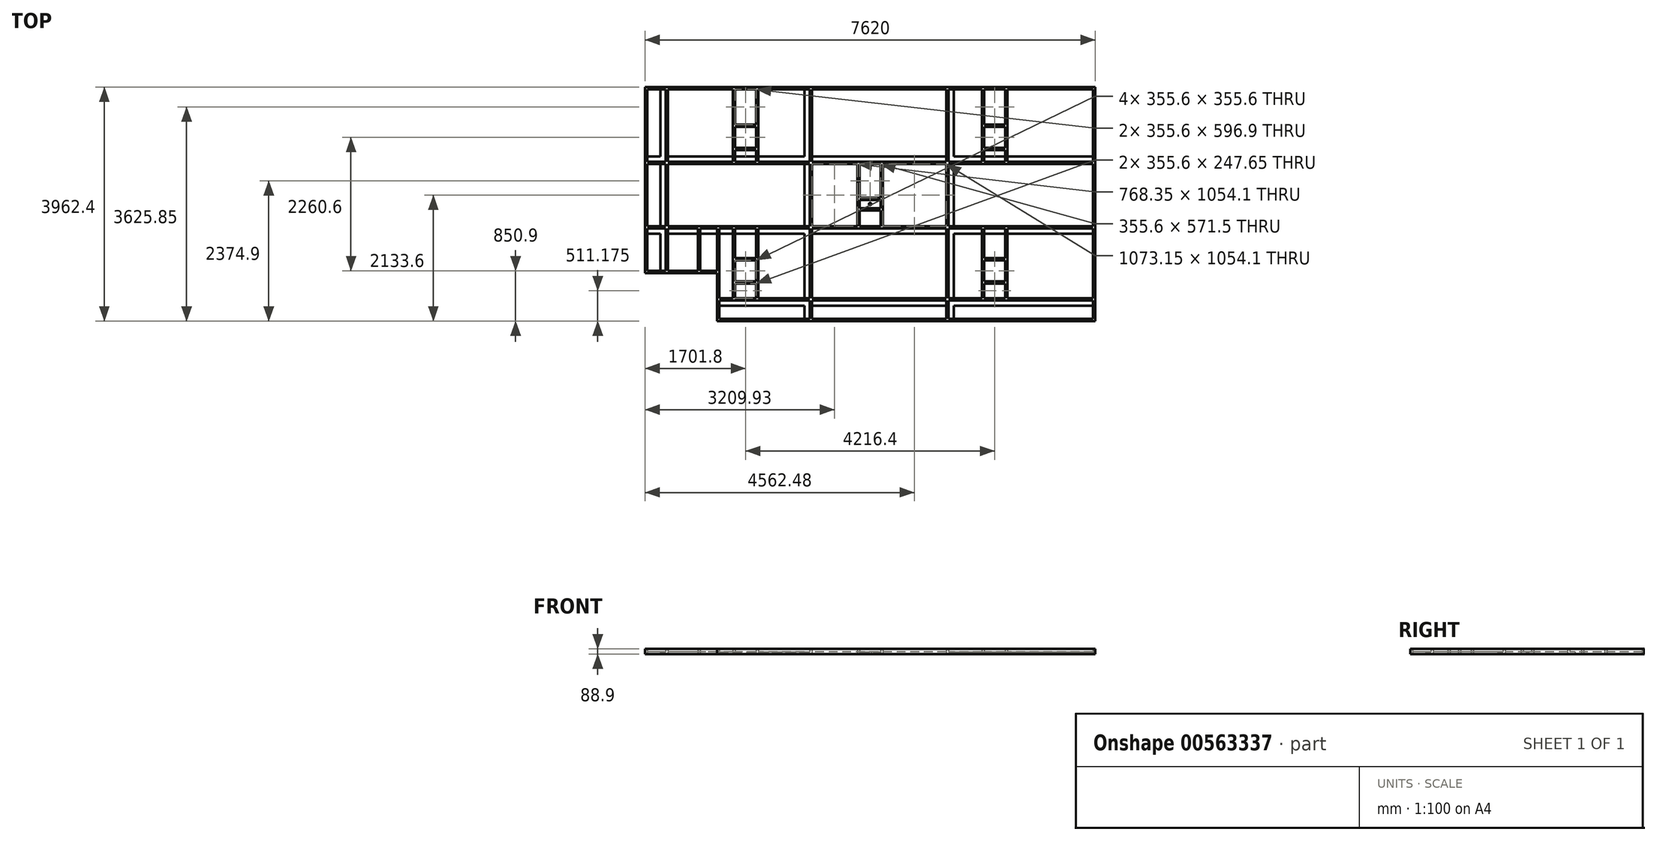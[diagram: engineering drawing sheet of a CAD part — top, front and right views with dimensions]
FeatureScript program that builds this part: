
annotation { "Feature Type Name" : "Feature", "Feature Type Description" : "" }
export const myFeature = defineFeature(function(context is Context, id is Id, definition is map)
    precondition{}
    {
        {
            var Q0;
            Q0=qCreatedBy(makeId("Top.planeOp"),FACE);
            var sketch = newSketch(context, id + "F0", { "sketchPlane" : qUnion([Q0])});
            skLineSegment(sketch, "E0", {"start": v(-2590.8, -1168.4) * mm, "end": v(-3810, -1168.4) * mm});
            skLineSegment(sketch, "E1", {"start": v(-3810, -1168.4) * mm, "end": v(-3810, 1981.2) * mm});
            skLineSegment(sketch, "E2", {"start": v(-3810, 1981.2) * mm, "end": v(3810, 1981.2) * mm});
            skLineSegment(sketch, "E3", {"start": v(3810, 1981.2) * mm, "end": v(3810, -1981.2) * mm});
            skLineSegment(sketch, "E4", {"start": v(3810, -1981.2) * mm, "end": v(-2590.8, -1981.2) * mm});
            skLineSegment(sketch, "E5", {"start": v(-2590.8, -1981.2) * mm, "end": v(-2590.8, -1168.4) * mm});
            skLineSegment(sketch, "E6", {"start": v(0, 0) * mm, "end": v(0, 3581.3) * mm, "construction": true});
            skLineSegment(sketch, "E7", {"start": v(0, 0) * mm, "end": v(6897.1, 0) * mm, "construction": true});
            skLineSegment(sketch, "E8", {"start": v(3810, 762) * mm, "end": v(-3810, 762) * mm, "construction": true});
            skLineSegment(sketch, "E9", {"start": v(3810, -457.2) * mm, "end": v(-3810, -457.2) * mm, "construction": true});
            skLineSegment(sketch, "E10", {"start": v(-2590.8, -1676.4) * mm, "end": v(3810, -1676.4) * mm, "construction": true});
            skLineSegment(sketch, "E11.0", {"start": v(3771.9, 806.45) * mm, "end": v(1416.05, 806.45) * mm});
            skLineSegment(sketch, "E12.0", {"start": v(3771.9, 717.55) * mm, "end": v(1416.05, 717.55) * mm});
            skLineSegment(sketch, "E13.0", {"start": v(3771.9, -501.65) * mm, "end": v(1416.05, -501.65) * mm});
            skLineSegment(sketch, "E14.0", {"start": v(3771.9, -412.75) * mm, "end": v(1416.05, -412.75) * mm});
            skLineSegment(sketch, "E15.0", {"start": v(-2590.8, -1720.85) * mm, "end": v(-1111.25, -1720.85) * mm});
            skLineSegment(sketch, "E16.0", {"start": v(-2590.8, -1631.95) * mm, "end": v(-1111.25, -1631.95) * mm});
            skLineSegment(sketch, "E17.0", {"start": v(-3810, 1943.1) * mm, "end": v(3771.9, 1943.1) * mm});
            skLineSegment(sketch, "E18.0", {"start": v(3771.9, 1943.1) * mm, "end": v(3771.9, -1943.1) * mm});
            skLineSegment(sketch, "E19.0", {"start": v(3771.9, -1943.1) * mm, "end": v(-2590.8, -1943.1) * mm});
            skLineSegment(sketch, "E20", {"start": v(1371.6, 1943.1) * mm, "end": v(1371.6, -1943.1) * mm, "construction": true});
            skLineSegment(sketch, "E21", {"start": v(3771.9, -1943.1) * mm, "end": v(3810, -1943.1) * mm});
            skLineSegment(sketch, "E22", {"start": v(3771.9, 1943.1) * mm, "end": v(3810, 1943.1) * mm});
            skLineSegment(sketch, "E23.0", {"start": v(-1066.8, 1943.1) * mm, "end": v(-1066.8, -1943.1) * mm, "construction": true});
            skLineSegment(sketch, "E24.0", {"start": v(-3505.2, 1943.1) * mm, "end": v(-3505.2, -1168.4) * mm, "construction": true});
            skLineSegment(sketch, "E25.0", {"start": v(-1111.25, 1943.1) * mm, "end": v(-1111.25, -1943.1) * mm});
            skLineSegment(sketch, "E26.0", {"start": v(-1022.35, 1943.1) * mm, "end": v(-1022.35, -1943.1) * mm});
            skLineSegment(sketch, "E27.0", {"start": v(1327.15, 1943.1) * mm, "end": v(1327.15, -1943.1) * mm});
            skLineSegment(sketch, "E28.0", {"start": v(1416.05, 1943.1) * mm, "end": v(1416.05, -1943.1) * mm});
            skLineSegment(sketch, "E29.0", {"start": v(-3549.65, 1943.1) * mm, "end": v(-3549.65, -1168.4) * mm});
            skLineSegment(sketch, "E30.0", {"start": v(-3460.75, 1943.1) * mm, "end": v(-3460.75, -1168.4) * mm});
            skLineSegment(sketch, "E31.trimOffspring", {"start": v(-1111.25, 806.45) * mm, "end": v(-3460.75, 806.45) * mm});
            skLineSegment(sketch, "E32.trimOffspring", {"start": v(-1111.25, 717.55) * mm, "end": v(-3460.75, 717.55) * mm});
            skLineSegment(sketch, "E33.trimOffspring", {"start": v(-1111.25, -412.75) * mm, "end": v(-3460.75, -412.75) * mm});
            skLineSegment(sketch, "E34.trimOffspring", {"start": v(-1111.25, -501.65) * mm, "end": v(-3460.75, -501.65) * mm});
            skLineSegment(sketch, "E35.trimOffspring", {"start": v(-1022.35, -1631.95) * mm, "end": v(1327.15, -1631.95) * mm});
            skLineSegment(sketch, "E36.trimOffspring", {"start": v(-1022.35, -1720.85) * mm, "end": v(1327.15, -1720.85) * mm});
            skLineSegment(sketch, "E37.trimOffspring", {"start": v(1289.05, 806.45) * mm, "end": v(-984.25, 806.45) * mm});
            skLineSegment(sketch, "E38.trimOffspring", {"start": v(1289.05, 717.55) * mm, "end": v(-984.25, 717.55) * mm});
            skLineSegment(sketch, "E39.trimOffspring", {"start": v(1327.15, -412.75) * mm, "end": v(-984.25, -412.75) * mm});
            skLineSegment(sketch, "E40.trimOffspring", {"start": v(1327.15, -501.65) * mm, "end": v(-984.25, -501.65) * mm});
            skLineSegment(sketch, "E41.trimOffspring", {"start": v(1416.05, -1631.95) * mm, "end": v(3771.9, -1631.95) * mm});
            skLineSegment(sketch, "E42.trimOffspring", {"start": v(1416.05, -1720.85) * mm, "end": v(3771.9, -1720.85) * mm});
            skLineSegment(sketch, "E43.trimOffspring", {"start": v(-3549.65, -412.75) * mm, "end": v(-3810, -412.75) * mm});
            skLineSegment(sketch, "E44.trimOffspring", {"start": v(-3549.65, -501.65) * mm, "end": v(-3810, -501.65) * mm});
            skLineSegment(sketch, "E45.trimOffspring", {"start": v(-3549.65, 806.45) * mm, "end": v(-3810, 806.45) * mm});
            skLineSegment(sketch, "E46.trimOffspring", {"start": v(-3549.65, 717.55) * mm, "end": v(-3810, 717.55) * mm});
            skLineSegment(sketch, "E47.0", {"start": v(-3771.9, -1130.3) * mm, "end": v(-3771.9, 1981.2) * mm});
            skLineSegment(sketch, "E47.1", {"start": v(-2552.7, -1130.3) * mm, "end": v(-3771.9, -1130.3) * mm});
            skLineSegment(sketch, "E47.2", {"start": v(-2552.7, -1981.2) * mm, "end": v(-2552.7, -1130.3) * mm});
            skLineSegment(sketch, "E48.0", {"start": v(-984.25, 1943.1) * mm, "end": v(-984.25, -1943.1) * mm});
            skLineSegment(sketch, "E49.0", {"start": v(3771.9, 679.45) * mm, "end": v(1416.05, 679.45) * mm});
            skLineSegment(sketch, "E50.0", {"start": v(1289.05, 679.45) * mm, "end": v(-984.25, 679.45) * mm});
            skLineSegment(sketch, "E51.0", {"start": v(1289.05, 1943.1) * mm, "end": v(1289.05, -1943.1) * mm});
            skLineSegment(sketch, "E52.0", {"start": v(-1111.25, 679.45) * mm, "end": v(-3397.25, 679.45) * mm});
            skLineSegment(sketch, "E53.0", {"start": v(-3549.65, 679.45) * mm, "end": v(-3810, 679.45) * mm});
            skLineSegment(sketch, "E54.0", {"start": v(1327.15, -374.65) * mm, "end": v(-984.25, -374.65) * mm});
            skLineSegment(sketch, "E55.0", {"start": v(3771.9, -374.65) * mm, "end": v(1416.05, -374.65) * mm});
            skLineSegment(sketch, "E56.0", {"start": v(-1111.25, -374.65) * mm, "end": v(-3397.25, -374.65) * mm});
            skLineSegment(sketch, "E57", {"start": v(-3549.65, 717.55) * mm, "end": v(-3460.75, 717.55) * mm});
            skLineSegment(sketch, "E58", {"start": v(-3549.65, 679.45) * mm, "end": v(-3397.25, 679.45) * mm});
            skLineSegment(sketch, "E59", {"start": v(-3549.65, -374.65) * mm, "end": v(-3810, -374.65) * mm});
            skLineSegment(sketch, "E60.0", {"start": v(-2590.8, -1593.85) * mm, "end": v(-1111.25, -1593.85) * mm});
            skLineSegment(sketch, "E61.0", {"start": v(-1022.35, -1593.85) * mm, "end": v(1327.15, -1593.85) * mm});
            skLineSegment(sketch, "E62.0", {"start": v(1416.05, -1593.85) * mm, "end": v(3771.9, -1593.85) * mm});
            skLineSegment(sketch, "E63", {"start": v(-3549.65, -374.65) * mm, "end": v(-3397.25, -374.65) * mm});
            skLineSegment(sketch, "E64", {"start": v(-3549.65, -412.75) * mm, "end": v(-3460.75, -412.75) * mm});
            skLineSegment(sketch, "E65", {"start": v(-1111.25, -374.65) * mm, "end": v(-984.25, -374.65) * mm});
            skLineSegment(sketch, "E66", {"start": v(-1111.25, -412.75) * mm, "end": v(-984.25, -412.75) * mm});
            skLineSegment(sketch, "E67", {"start": v(-1111.25, 679.45) * mm, "end": v(-984.25, 679.45) * mm});
            skLineSegment(sketch, "E68", {"start": v(-984.25, 717.55) * mm, "end": v(-1111.25, 717.55) * mm});
            skLineSegment(sketch, "E69", {"start": v(1289.05, 679.45) * mm, "end": v(1416.05, 679.45) * mm});
            skLineSegment(sketch, "E70", {"start": v(1289.05, 717.55) * mm, "end": v(1416.05, 717.55) * mm});
            skLineSegment(sketch, "E71", {"start": v(1327.15, -374.65) * mm, "end": v(1416.05, -374.65) * mm});
            skLineSegment(sketch, "E72", {"start": v(1327.15, -412.75) * mm, "end": v(1416.05, -412.75) * mm});
            skLineSegment(sketch, "E73", {"start": v(1327.15, -1593.85) * mm, "end": v(1416.05, -1593.85) * mm});
            skLineSegment(sketch, "E74", {"start": v(1327.15, -1631.95) * mm, "end": v(1416.05, -1631.95) * mm});
            skLineSegment(sketch, "E75", {"start": v(-1111.25, -1593.85) * mm, "end": v(-1022.35, -1593.85) * mm});
            skLineSegment(sketch, "E76", {"start": v(-1111.25, -1631.95) * mm, "end": v(-1022.35, -1631.95) * mm});
            skLineSegment(sketch, "E77.0", {"start": v(-3422.65, 1943.1) * mm, "end": v(-3422.65, -1168.4) * mm});
            skLineSegment(sketch, "E78", {"start": v(2108.2, 1943.1) * mm, "end": v(2108.2, -1177.77) * mm, "construction": true});
            skLineSegment(sketch, "E79", {"start": v(0, 0) * mm, "end": v(-3916.53, 0) * mm, "construction": true});
            skLineSegment(sketch, "E80", {"start": v(-2108.2, 1943.1) * mm, "end": v(-2108.2, -1130.3) * mm, "construction": true});
            skLineSegment(sketch, "E81", {"start": v(-2552.7, -1130.3) * mm, "end": v(3771.9, -1130.3) * mm, "construction": true});
            skLineSegment(sketch, "E82", {"start": v(-3422.65, 1130.3) * mm, "end": v(3771.9, 1130.3) * mm, "construction": true});
            skLineSegment(sketch, "E83", {"start": v(-3771.9, -317.5) * mm, "end": v(-3104.94, -317.5) * mm, "construction": true});
            skCircle(sketch, "E84", {"center": v(-2108.2, 1130.3) * mm, "radius": 82.55 * mm});
            skCircle(sketch, "E85", {"center": v(-2108.2, -1130.3) * mm, "radius": 82.55 * mm});
            skCircle(sketch, "E86", {"center": v(2108.2, 1130.3) * mm, "radius": 82.55 * mm});
            skCircle(sketch, "E87", {"center": v(2108.2, -1130.3) * mm, "radius": 82.55 * mm});
            skLineSegment(sketch, "E88", {"start": v(-2286, -1593.85) * mm, "end": v(-2286, -501.65) * mm});
            skLineSegment(sketch, "E89", {"start": v(-1930.4, -501.65) * mm, "end": v(-1930.4, -1593.85) * mm});
            skLineSegment(sketch, "E90.bottom", {"start": v(-2286, -1308.1) * mm, "end": v(-1930.4, -1308.1) * mm});
            skLineSegment(sketch, "E90.top", {"start": v(-2286, -952.5) * mm, "end": v(-1930.4, -952.5) * mm});
            skLineSegment(sketch, "E90.left", {"start": v(-2286, -1308.1) * mm, "end": v(-2286, -952.5) * mm});
            skLineSegment(sketch, "E90.right", {"start": v(-1930.4, -1308.1) * mm, "end": v(-1930.4, -952.5) * mm});
            skLineSegment(sketch, "E91.0", {"start": v(-2324.1, -1593.85) * mm, "end": v(-2324.1, -501.65) * mm});
            skLineSegment(sketch, "E92.0", {"start": v(-1892.3, -501.65) * mm, "end": v(-1892.3, -1593.85) * mm});
            skLineSegment(sketch, "E93.0", {"start": v(-2286, -914.4) * mm, "end": v(-1930.4, -914.4) * mm});
            skLineSegment(sketch, "E94.0", {"start": v(-2286, -1346.2) * mm, "end": v(-1930.4, -1346.2) * mm});
            skLineSegment(sketch, "E95", {"start": v(-2324.1, -501.65) * mm, "end": v(-2324.1, -412.75) * mm});
            skLineSegment(sketch, "E96", {"start": v(-2286, -501.65) * mm, "end": v(-2286, -412.75) * mm});
            skLineSegment(sketch, "E97", {"start": v(-1930.4, -501.65) * mm, "end": v(-1930.4, -412.75) * mm});
            skLineSegment(sketch, "E98", {"start": v(-1892.3, -501.65) * mm, "end": v(-1892.3, -412.75) * mm});
            skLineSegment(sketch, "E99", {"start": v(-2324.1, 717.55) * mm, "end": v(-2324.1, 1943.1) * mm});
            skLineSegment(sketch, "E100.0", {"start": v(-2286, 717.55) * mm, "end": v(-2286, 1943.1) * mm});
            skLineSegment(sketch, "E101.0", {"start": v(-1930.4, 717.55) * mm, "end": v(-1930.4, 1943.1) * mm});
            skLineSegment(sketch, "E102.0", {"start": v(-1892.3, 717.55) * mm, "end": v(-1892.3, 1943.1) * mm});
            skLineSegment(sketch, "E103", {"start": v(-2286, 1308.1) * mm, "end": v(-1930.4, 1308.1) * mm});
            skLineSegment(sketch, "E104", {"start": v(-2286, 952.5) * mm, "end": v(-1930.4, 952.5) * mm});
            skLineSegment(sketch, "E105.0", {"start": v(-2286, 1346.2) * mm, "end": v(-1930.4, 1346.2) * mm});
            skLineSegment(sketch, "E106.0", {"start": v(-2286, 914.4) * mm, "end": v(-1930.4, 914.4) * mm});
            skLineSegment(sketch, "E107", {"start": v(1930.4, 806.45) * mm, "end": v(1930.4, 1943.1) * mm});
            skLineSegment(sketch, "E108.0", {"start": v(2286, 717.55) * mm, "end": v(2286, 1943.1) * mm});
            skLineSegment(sketch, "E109.0", {"start": v(2324.1, 717.55) * mm, "end": v(2324.1, 1943.1) * mm});
            skLineSegment(sketch, "E110.0", {"start": v(1892.3, 717.55) * mm, "end": v(1892.3, 1943.1) * mm});
            skLineSegment(sketch, "E111", {"start": v(1930.4, 806.45) * mm, "end": v(1930.4, 717.55) * mm});
            skLineSegment(sketch, "E112", {"start": v(1930.4, 1308.1) * mm, "end": v(2286, 1308.1) * mm});
            skLineSegment(sketch, "E113.0", {"start": v(1930.4, 952.5) * mm, "end": v(2286, 952.5) * mm});
            skLineSegment(sketch, "E114.0", {"start": v(1930.4, 1346.2) * mm, "end": v(2286, 1346.2) * mm});
            skLineSegment(sketch, "E115.0", {"start": v(1930.4, 914.4) * mm, "end": v(2286, 914.4) * mm});
            skLineSegment(sketch, "E116", {"start": v(1930.4, -501.65) * mm, "end": v(1930.4, -1593.85) * mm});
            skLineSegment(sketch, "E117", {"start": v(2286, -501.65) * mm, "end": v(2286, -1593.85) * mm});
            skLineSegment(sketch, "E118", {"start": v(1930.4, -1308.1) * mm, "end": v(2286, -1308.1) * mm});
            skLineSegment(sketch, "E119", {"start": v(1930.4, -952.5) * mm, "end": v(2286, -952.5) * mm});
            skLineSegment(sketch, "E120.0", {"start": v(1892.3, -501.65) * mm, "end": v(1892.3, -1593.85) * mm});
            skLineSegment(sketch, "E121.0", {"start": v(2324.1, -501.65) * mm, "end": v(2324.1, -1593.85) * mm});
            skLineSegment(sketch, "E122.0", {"start": v(1930.4, -914.4) * mm, "end": v(2286, -914.4) * mm});
            skLineSegment(sketch, "E123.0", {"start": v(1930.4, -1346.2) * mm, "end": v(2286, -1346.2) * mm});
            skLineSegment(sketch, "E124", {"start": v(-177.8, 679.45) * mm, "end": v(-177.8, -374.65) * mm});
            skLineSegment(sketch, "E125", {"start": v(177.8, 679.45) * mm, "end": v(177.8, -374.65) * mm});
            skLineSegment(sketch, "E126.0", {"start": v(-215.9, 679.45) * mm, "end": v(-215.9, -374.65) * mm});
            skLineSegment(sketch, "E127.0", {"start": v(215.9, 679.45) * mm, "end": v(215.9, -374.65) * mm});
            skLineSegment(sketch, "E128", {"start": v(-177.8, 69.85) * mm, "end": v(177.8, 69.85) * mm});
            skLineSegment(sketch, "E129", {"start": v(-177.8, -69.85) * mm, "end": v(177.8, -69.85) * mm});
            skLineSegment(sketch, "E130.0", {"start": v(-177.8, 107.95) * mm, "end": v(177.8, 107.95) * mm});
            skLineSegment(sketch, "E131.0", {"start": v(-177.8, -107.95) * mm, "end": v(177.8, -107.95) * mm});
            skCircle(sketch, "E132", {"center": v(0, 0) * mm, "radius": 19.05 * mm});
            skLineSegment(sketch, "E133", {"start": v(1892.3, -501.65) * mm, "end": v(1892.3, -412.75) * mm});
            skLineSegment(sketch, "E134", {"start": v(1930.4, -501.65) * mm, "end": v(1930.4, -412.75) * mm});
            skLineSegment(sketch, "E135", {"start": v(2324.1, -501.65) * mm, "end": v(2324.1, -412.75) * mm});
            skLineSegment(sketch, "E136", {"start": v(2286, -501.65) * mm, "end": v(2286, -412.75) * mm});
            skLineSegment(sketch, "E137", {"start": v(-2552.7, -1130.3) * mm, "end": v(-2552.7, -412.75) * mm});
            skLineSegment(sketch, "E138", {"start": v(-2590.8, -1168.4) * mm, "end": v(-2590.8, -412.75) * mm});
            skLineSegment(sketch, "E139", {"start": v(-2914.65, -1130.3) * mm, "end": v(-2914.65, -412.75) * mm});
            skLineSegment(sketch, "E140.0", {"start": v(-2876.55, -1130.3) * mm, "end": v(-2876.55, -412.75) * mm});
            skSolve(sketch);
        }
        {
            var Q0;
            {var subQ1=sQuery(id+"F0.wireOp",EDGE,"E47.1");var subQ4=makeQuery(id+"F0.imprint","INTERSECT",VERTEX,{"derivedFrom":[subQ1,sQuery(id+"F0.wireOp",EDGE,"E139")]});var subQ7=sQuery(id+"F0.wireOp",EDGE,"E5");var subQ8=sQuery(id+"F0.wireOp",EDGE,"E0");var subQ13=sQuery(id+"F0.wireOp",EDGE,"E43.trimOffspring");var subQ14=sQuery(id+"F0.wireOp",EDGE,"E1");var subQ15=makeQuery(id+"F0.imprint","INTERSECT",VERTEX,{"derivedFrom":[subQ14,subQ13]});var subQ23=sQuery(id+"F0.wireOp",EDGE,"E2");var subQ24=makeQuery(id+"F0.imprint","INTERSECT",VERTEX,{"derivedFrom":[subQ14,subQ23]});var subQ31=sQuery(id+"F0.wireOp",EDGE,"E53.0");var subQ32=makeQuery(id+"F0.imprint","INTERSECT",VERTEX,{"derivedFrom":[subQ14,subQ31]});var subQ39=sQuery(id+"F0.wireOp",EDGE,"E19.0");var subQ40=makeQuery(id+"F0.imprint","INTERSECT",VERTEX,{"derivedFrom":[subQ7,subQ39]});var subQ41=sQuery(id+"F0.wireOp",EDGE,"E15.0");var subQ42=makeQuery(id+"F0.imprint","INTERSECT",VERTEX,{"derivedFrom":[subQ7,subQ41]});var subQ48=sQuery(id+"F0.wireOp",EDGE,"E46.trimOffspring");var subQ49=makeQuery(id+"F0.imprint","INTERSECT",VERTEX,{"derivedFrom":[subQ14,subQ48]});var subQ52=sQuery(id+"F0.wireOp",EDGE,"E21");var subQ53=makeQuery(id+"F0.imprint","IMPRINT",EDGE,{"derivedFrom":subQ52});var subQ54=sQuery(id+"F0.wireOp",EDGE,"E4");var subQ74=sQuery(id+"F0.wireOp",EDGE,"E45.trimOffspring");var subQ75=makeQuery(id+"F0.imprint","INTERSECT",VERTEX,{"derivedFrom":[subQ14,subQ74]});var subQ90=sQuery(id+"F0.wireOp",EDGE,"E22");var subQ94=makeQuery(id+"F0.imprint","IMPRINT",EDGE,{"derivedFrom":subQ90});var subQ95=sQuery(id+"F0.wireOp",EDGE,"E30.0");var subQ96=makeQuery(id+"F0.imprint","INTERSECT",VERTEX,{"derivedFrom":[subQ8,subQ95]});var subQ99=sQuery(id+"F0.wireOp",EDGE,"E60.0");var subQ100=makeQuery(id+"F0.imprint","INTERSECT",VERTEX,{"derivedFrom":[subQ7,subQ99]});var subQ102=makeQuery(id+"F0.imprint","IMPRINT",EDGE,{"disambiguationData":[TD([[subQ100,-1.0]])],"derivedFrom":subQ99});var subQ103=sQuery(id+"F0.wireOp",EDGE,"E29.0");var subQ104=makeQuery(id+"F0.imprint","INTERSECT",VERTEX,{"derivedFrom":[subQ8,subQ103]});var subQ110=makeQuery(id+"F0.imprint","INTERSECT",VERTEX,{"derivedFrom":[subQ54,subQ7]});Q0=qUnion([makeQuery(id+"F0.imprint","IMPRINT",FACE,{"disambiguationData":[TD([[subQ94,1.0]])]}),makeQuery(id+"F0.imprint","IMPRINT",FACE,{"disambiguationData":[TD([[makeQuery(id+"F0.imprint","IMPRINT",EDGE,{"disambiguationData":[TD([[subQ110,1.0]])],"derivedFrom":subQ54}),-1.0]])]}),makeQuery(id+"F0.imprint","IMPRINT",FACE,{"disambiguationData":[TD([[subQ102,1.0]])]}),makeQuery(id+"F0.imprint","IMPRINT",FACE,{"disambiguationData":[TD([[makeQuery(id+"F0.imprint","IMPRINT",EDGE,{"disambiguationData":[TD([[subQ104,-1.0]])],"derivedFrom":subQ8}),-1.0]])]}),makeQuery(id+"F0.imprint","IMPRINT",FACE,{"disambiguationData":[TD([[makeQuery(id+"F0.imprint","IMPRINT",EDGE,{"disambiguationData":[TD([[subQ96,-1.0]])],"derivedFrom":subQ8}),-1.0]])]}),makeQuery(id+"F0.imprint","IMPRINT",FACE,{"disambiguationData":[TD([[makeQuery(id+"F0.imprint","IMPRINT",EDGE,{"disambiguationData":[TD([[subQ15,-1.0]])],"derivedFrom":subQ14}),-1.0]])]}),makeQuery(id+"F0.imprint","IMPRINT",FACE,{"disambiguationData":[TD([[makeQuery(id+"F0.imprint","IMPRINT",EDGE,{"disambiguationData":[TD([[subQ100,1.0]])],"derivedFrom":subQ7}),-1.0]])]}),makeQuery(id+"F0.imprint","IMPRINT",FACE,{"disambiguationData":[TD([[makeQuery(id+"F0.imprint","IMPRINT",EDGE,{"disambiguationData":[TD([[subQ96,1.0]])],"derivedFrom":subQ8}),-1.0]])]}),makeQuery(id+"F0.imprint","IMPRINT",FACE,{"disambiguationData":[TD([[subQ53,1.0]])]}),makeQuery(id+"F0.imprint","IMPRINT",FACE,{"disambiguationData":[TD([[makeQuery(id+"F0.imprint","IMPRINT",EDGE,{"disambiguationData":[TD([[subQ75,1.0]])],"derivedFrom":subQ14}),-1.0]])]}),makeQuery(id+"F0.imprint","IMPRINT",FACE,{"disambiguationData":[TD([[makeQuery(id+"F0.imprint","IMPRINT",EDGE,{"disambiguationData":[TD([[subQ42,-1.0]])],"derivedFrom":subQ7}),-1.0]])]}),makeQuery(id+"F0.imprint","IMPRINT",FACE,{"disambiguationData":[TD([[makeQuery(id+"F0.imprint","IMPRINT",EDGE,{"disambiguationData":[TD([[subQ75,-1.0]])],"derivedFrom":subQ14}),-1.0]])]}),makeQuery(id+"F0.imprint","IMPRINT",FACE,{"disambiguationData":[TD([[subQ53,-1.0]])]}),makeQuery(id+"F0.imprint","IMPRINT",FACE,{"disambiguationData":[TD([[makeQuery(id+"F0.imprint","IMPRINT",EDGE,{"disambiguationData":[TD([[subQ49,1.0]])],"derivedFrom":subQ14}),-1.0]])]}),makeQuery(id+"F0.imprint","IMPRINT",FACE,{"disambiguationData":[TD([[makeQuery(id+"F0.imprint","IMPRINT",EDGE,{"disambiguationData":[TD([[subQ40,-1.0]])],"derivedFrom":subQ7}),-1.0]])]}),makeQuery(id+"F0.imprint","IMPRINT",FACE,{"disambiguationData":[TD([[makeQuery(id+"F0.imprint","IMPRINT",EDGE,{"disambiguationData":[TD([[subQ32,1.0]])],"derivedFrom":subQ14}),-1.0]])]}),makeQuery(id+"F0.imprint","IMPRINT",FACE,{"disambiguationData":[TD([[makeQuery(id+"F0.imprint","IMPRINT",EDGE,{"disambiguationData":[TD([[subQ24,1.0]])],"derivedFrom":subQ14}),-1.0]])]}),makeQuery(id+"F0.imprint","IMPRINT",FACE,{"disambiguationData":[TD([[makeQuery(id+"F0.imprint","IMPRINT",EDGE,{"disambiguationData":[TD([[subQ15,1.0]])],"derivedFrom":subQ14}),-1.0]])]}),makeQuery(id+"F0.imprint","IMPRINT",FACE,{"disambiguationData":[TD([[makeQuery(id+"F0.imprint","IMPRINT",EDGE,{"disambiguationData":[TD([[subQ4,-1.0]])],"derivedFrom":subQ1}),1.0]])]})]);}
            var Q1;
            {var subQ6=sQuery(id+"F0.wireOp",EDGE,"E126.0");Q1=makeQuery(id+"F0.imprint","IMPRINT",FACE,{"disambiguationData":[TD([[makeQuery(id+"F0.imprint","IMPRINT",EDGE,{"derivedFrom":subQ6}),1.0]])]});}
            var Q2;
            {var subQ7=sQuery(id+"F0.wireOp",EDGE,"E127.0");Q2=makeQuery(id+"F0.imprint","IMPRINT",FACE,{"disambiguationData":[TD([[makeQuery(id+"F0.imprint","IMPRINT",EDGE,{"derivedFrom":subQ7}),-1.0]])]});}
            var Q3;
            {var subQ0=sQuery(id+"F0.wireOp",EDGE,"E128");Q3=makeQuery(id+"F0.imprint","IMPRINT",FACE,{"disambiguationData":[TD([[makeQuery(id+"F0.imprint","IMPRINT",EDGE,{"derivedFrom":subQ0}),1.0]])]});}
            var Q4;
            {var subQ0=sQuery(id+"F0.wireOp",EDGE,"E129");Q4=makeQuery(id+"F0.imprint","IMPRINT",FACE,{"disambiguationData":[TD([[makeQuery(id+"F0.imprint","IMPRINT",EDGE,{"derivedFrom":subQ0}),-1.0]])]});}
            var Q5;
            {var subQ0=sQuery(id+"F0.wireOp",EDGE,"E51.0");var subQ1=sQuery(id+"F0.wireOp",EDGE,"E39.trimOffspring");var subQ2=makeQuery(id+"F0.imprint","INTERSECT",VERTEX,{"derivedFrom":[subQ1,subQ0]});Q5=makeQuery(id+"F0.imprint","IMPRINT",FACE,{"disambiguationData":[TD([[makeQuery(id+"F0.imprint","IMPRINT",EDGE,{"disambiguationData":[TD([[subQ2,1.0]])],"derivedFrom":subQ0}),-1.0]])]});}
            var Q6;
            {var subQ3=sQuery(id+"F0.wireOp",EDGE,"E39.trimOffspring");var subQ5=sQuery(id+"F0.wireOp",EDGE,"E51.0");var subQ7=makeQuery(id+"F0.imprint","INTERSECT",VERTEX,{"derivedFrom":[subQ3,subQ5]});Q6=makeQuery(id+"F0.imprint","IMPRINT",FACE,{"disambiguationData":[TD([[makeQuery(id+"F0.imprint","IMPRINT",EDGE,{"disambiguationData":[TD([[subQ7,1.0]])],"derivedFrom":subQ5}),1.0]])]});}
            var Q7;
            {var subQ0=sQuery(id+"F0.wireOp",EDGE,"E71");Q7=makeQuery(id+"F0.imprint","IMPRINT",FACE,{"disambiguationData":[TD([[makeQuery(id+"F0.imprint","IMPRINT",EDGE,{"derivedFrom":subQ0}),-1.0]])]});}
            var Q8;
            {var subQ5=sQuery(id+"F0.wireOp",EDGE,"E55.0");Q8=makeQuery(id+"F0.imprint","IMPRINT",FACE,{"disambiguationData":[TD([[makeQuery(id+"F0.imprint","IMPRINT",EDGE,{"derivedFrom":subQ5}),1.0]])]});}
            var Q9;
            {var subQ0=sQuery(id+"F0.wireOp",EDGE,"E69");var subQ1=sQuery(id+"F0.wireOp",EDGE,"E27.0");var subQ2=makeQuery(id+"F0.imprint","INTERSECT",VERTEX,{"derivedFrom":[subQ1,subQ0]});Q9=makeQuery(id+"F0.imprint","IMPRINT",FACE,{"disambiguationData":[TD([[makeQuery(id+"F0.imprint","IMPRINT",EDGE,{"disambiguationData":[TD([[subQ2,-1.0]])],"derivedFrom":subQ1}),-1.0]])]});}
            var Q10;
            {var subQ7=sQuery(id+"F0.wireOp",EDGE,"E38.trimOffspring");Q10=makeQuery(id+"F0.imprint","IMPRINT",FACE,{"disambiguationData":[TD([[makeQuery(id+"F0.imprint","IMPRINT",EDGE,{"derivedFrom":subQ7}),1.0]])]});}
            var Q11;
            {var subQ0=sQuery(id+"F0.wireOp",EDGE,"E69");var subQ1=sQuery(id+"F0.wireOp",EDGE,"E27.0");var subQ2=makeQuery(id+"F0.imprint","INTERSECT",VERTEX,{"derivedFrom":[subQ1,subQ0]});Q11=makeQuery(id+"F0.imprint","IMPRINT",FACE,{"disambiguationData":[TD([[makeQuery(id+"F0.imprint","IMPRINT",EDGE,{"disambiguationData":[TD([[subQ2,1.0]])],"derivedFrom":subQ1}),-1.0]])]});}
            var Q12;
            {var subQ0=sQuery(id+"F0.wireOp",EDGE,"E69");var subQ1=sQuery(id+"F0.wireOp",EDGE,"E27.0");var subQ2=makeQuery(id+"F0.imprint","INTERSECT",VERTEX,{"derivedFrom":[subQ1,subQ0]});Q12=makeQuery(id+"F0.imprint","IMPRINT",FACE,{"disambiguationData":[TD([[makeQuery(id+"F0.imprint","IMPRINT",EDGE,{"disambiguationData":[TD([[subQ2,1.0]])],"derivedFrom":subQ1}),1.0]])]});}
            var Q13;
            {var subQ5=sQuery(id+"F0.wireOp",EDGE,"E49.0");Q13=makeQuery(id+"F0.imprint","IMPRINT",FACE,{"disambiguationData":[TD([[makeQuery(id+"F0.imprint","IMPRINT",EDGE,{"derivedFrom":subQ5}),-1.0]])]});}
            var Q14;
            {var subQ4=sQuery(id+"F0.wireOp",EDGE,"E17.0");var subQ6=sQuery(id+"F0.wireOp",EDGE,"E27.0");var subQ7=makeQuery(id+"F0.imprint","INTERSECT",VERTEX,{"derivedFrom":[subQ4,subQ6]});Q14=makeQuery(id+"F0.imprint","IMPRINT",FACE,{"disambiguationData":[TD([[makeQuery(id+"F0.imprint","IMPRINT",EDGE,{"disambiguationData":[TD([[subQ7,1.0]])],"derivedFrom":subQ4}),-1.0]])]});}
            var Q15;
            {var subQ0=sQuery(id+"F0.wireOp",EDGE,"E68");var subQ1=sQuery(id+"F0.wireOp",EDGE,"E26.0");var subQ2=makeQuery(id+"F0.imprint","INTERSECT",VERTEX,{"derivedFrom":[subQ1,subQ0]});Q15=makeQuery(id+"F0.imprint","IMPRINT",FACE,{"disambiguationData":[TD([[makeQuery(id+"F0.imprint","IMPRINT",EDGE,{"disambiguationData":[TD([[subQ2,-1.0]])],"derivedFrom":subQ1}),1.0]])]});}
            var Q16;
            {var subQ0=sQuery(id+"F0.wireOp",EDGE,"E48.0");var subQ4=sQuery(id+"F0.wireOp",EDGE,"E17.0");var subQ5=makeQuery(id+"F0.imprint","INTERSECT",VERTEX,{"derivedFrom":[subQ4,subQ0]});Q16=makeQuery(id+"F0.imprint","IMPRINT",FACE,{"disambiguationData":[TD([[makeQuery(id+"F0.imprint","IMPRINT",EDGE,{"disambiguationData":[TD([[subQ5,1.0]])],"derivedFrom":subQ4}),-1.0]])]});}
            var Q17;
            {var subQ0=sQuery(id+"F0.wireOp",EDGE,"E67");var subQ1=sQuery(id+"F0.wireOp",EDGE,"E26.0");var subQ2=makeQuery(id+"F0.imprint","INTERSECT",VERTEX,{"derivedFrom":[subQ1,subQ0]});Q17=makeQuery(id+"F0.imprint","IMPRINT",FACE,{"disambiguationData":[TD([[makeQuery(id+"F0.imprint","IMPRINT",EDGE,{"disambiguationData":[TD([[subQ2,-1.0]])],"derivedFrom":subQ1}),1.0]])]});}
            var Q18;
            {var subQ0=sQuery(id+"F0.wireOp",EDGE,"E66");var subQ1=sQuery(id+"F0.wireOp",EDGE,"E26.0");var subQ2=makeQuery(id+"F0.imprint","INTERSECT",VERTEX,{"derivedFrom":[subQ1,subQ0]});Q18=makeQuery(id+"F0.imprint","IMPRINT",FACE,{"disambiguationData":[TD([[makeQuery(id+"F0.imprint","IMPRINT",EDGE,{"disambiguationData":[TD([[subQ2,1.0]])],"derivedFrom":subQ1}),1.0]])]});}
            var Q19;
            {var subQ0=sQuery(id+"F0.wireOp",EDGE,"E66");var subQ5=sQuery(id+"F0.wireOp",EDGE,"E26.0");var subQ6=makeQuery(id+"F0.imprint","INTERSECT",VERTEX,{"derivedFrom":[subQ5,subQ0]});Q19=makeQuery(id+"F0.imprint","IMPRINT",FACE,{"disambiguationData":[TD([[makeQuery(id+"F0.imprint","IMPRINT",EDGE,{"disambiguationData":[TD([[subQ6,1.0]])],"derivedFrom":subQ5}),-1.0]])]});}
            var Q20;
            {var subQ11=sQuery(id+"F0.wireOp",EDGE,"E56.0");Q20=makeQuery(id+"F0.imprint","IMPRINT",FACE,{"disambiguationData":[TD([[makeQuery(id+"F0.imprint","IMPRINT",EDGE,{"derivedFrom":subQ11}),1.0]])]});}
            var Q21;
            {var subQ1=sQuery(id+"F0.wireOp",EDGE,"E48.0");var subQ6=sQuery(id+"F0.wireOp",EDGE,"E61.0");var subQ8=makeQuery(id+"F0.imprint","INTERSECT",VERTEX,{"derivedFrom":[subQ1,subQ6]});Q21=makeQuery(id+"F0.imprint","IMPRINT",FACE,{"disambiguationData":[TD([[makeQuery(id+"F0.imprint","IMPRINT",EDGE,{"disambiguationData":[TD([[subQ8,1.0]])],"derivedFrom":subQ1}),-1.0]])]});}
            var Q22;
            {var subQ3=sQuery(id+"F0.wireOp",EDGE,"E40.trimOffspring");var subQ5=sQuery(id+"F0.wireOp",EDGE,"E51.0");var subQ7=makeQuery(id+"F0.imprint","INTERSECT",VERTEX,{"derivedFrom":[subQ3,subQ5]});Q22=makeQuery(id+"F0.imprint","IMPRINT",FACE,{"disambiguationData":[TD([[makeQuery(id+"F0.imprint","IMPRINT",EDGE,{"disambiguationData":[TD([[subQ7,1.0]])],"derivedFrom":subQ3}),-1.0]])]});}
            var Q23;
            {var subQ3=sQuery(id+"F0.wireOp",EDGE,"E40.trimOffspring");var subQ5=sQuery(id+"F0.wireOp",EDGE,"E51.0");var subQ6=makeQuery(id+"F0.imprint","INTERSECT",VERTEX,{"derivedFrom":[subQ3,subQ5]});Q23=makeQuery(id+"F0.imprint","IMPRINT",FACE,{"disambiguationData":[TD([[makeQuery(id+"F0.imprint","IMPRINT",EDGE,{"disambiguationData":[TD([[subQ6,1.0]])],"derivedFrom":subQ3}),1.0]])]});}
            var Q24;
            {var subQ3=sQuery(id+"F0.wireOp",EDGE,"E68");var subQ5=sQuery(id+"F0.wireOp",EDGE,"E26.0");var subQ7=makeQuery(id+"F0.imprint","INTERSECT",VERTEX,{"derivedFrom":[subQ5,subQ3]});Q24=makeQuery(id+"F0.imprint","IMPRINT",FACE,{"disambiguationData":[TD([[makeQuery(id+"F0.imprint","IMPRINT",EDGE,{"disambiguationData":[TD([[subQ7,-1.0]])],"derivedFrom":subQ5}),-1.0]])]});}
            var Q25;
            {var subQ9=sQuery(id+"F0.wireOp",EDGE,"E52.0");Q25=makeQuery(id+"F0.imprint","IMPRINT",FACE,{"disambiguationData":[TD([[makeQuery(id+"F0.imprint","IMPRINT",EDGE,{"derivedFrom":subQ9}),-1.0]])]});}
            var Q26;
            {var subQ0=sQuery(id+"F0.wireOp",EDGE,"E58");var subQ1=sQuery(id+"F0.wireOp",EDGE,"E30.0");var subQ2=makeQuery(id+"F0.imprint","INTERSECT",VERTEX,{"derivedFrom":[subQ1,subQ0]});Q26=makeQuery(id+"F0.imprint","IMPRINT",FACE,{"disambiguationData":[TD([[makeQuery(id+"F0.imprint","IMPRINT",EDGE,{"disambiguationData":[TD([[subQ2,-1.0]])],"derivedFrom":subQ1}),1.0]])]});}
            var Q27;
            {var subQ1=sQuery(id+"F0.wireOp",EDGE,"E30.0");var subQ3=sQuery(id+"F0.wireOp",EDGE,"E58");var subQ4=makeQuery(id+"F0.imprint","INTERSECT",VERTEX,{"derivedFrom":[subQ1,subQ3]});Q27=makeQuery(id+"F0.imprint","IMPRINT",FACE,{"disambiguationData":[TD([[makeQuery(id+"F0.imprint","IMPRINT",EDGE,{"disambiguationData":[TD([[subQ4,-1.0]])],"derivedFrom":subQ3}),1.0]])]});}
            var Q28;
            {var subQ0=sQuery(id+"F0.wireOp",EDGE,"E57");Q28=makeQuery(id+"F0.imprint","IMPRINT",FACE,{"disambiguationData":[TD([[makeQuery(id+"F0.imprint","IMPRINT",EDGE,{"derivedFrom":subQ0}),-1.0]])]});}
            var Q29;
            {var subQ0=sQuery(id+"F0.wireOp",EDGE,"E46.trimOffspring");var subQ5=sQuery(id+"F0.wireOp",EDGE,"E47.0");var subQ6=makeQuery(id+"F0.imprint","INTERSECT",VERTEX,{"derivedFrom":[subQ0,subQ5]});Q29=makeQuery(id+"F0.imprint","IMPRINT",FACE,{"disambiguationData":[TD([[makeQuery(id+"F0.imprint","IMPRINT",EDGE,{"disambiguationData":[TD([[subQ6,1.0]])],"derivedFrom":subQ5}),-1.0]])]});}
            var Q30;
            {var subQ0=sQuery(id+"F0.wireOp",EDGE,"E64");Q30=makeQuery(id+"F0.imprint","IMPRINT",FACE,{"disambiguationData":[TD([[makeQuery(id+"F0.imprint","IMPRINT",EDGE,{"derivedFrom":subQ0}),1.0]])]});}
            var Q31;
            {var subQ0=sQuery(id+"F0.wireOp",EDGE,"E43.trimOffspring");var subQ5=sQuery(id+"F0.wireOp",EDGE,"E47.0");var subQ6=makeQuery(id+"F0.imprint","INTERSECT",VERTEX,{"derivedFrom":[subQ0,subQ5]});Q31=makeQuery(id+"F0.imprint","IMPRINT",FACE,{"disambiguationData":[TD([[makeQuery(id+"F0.imprint","IMPRINT",EDGE,{"disambiguationData":[TD([[subQ6,-1.0]])],"derivedFrom":subQ5}),-1.0]])]});}
            var Q32;
            {var subQ1=sQuery(id+"F0.wireOp",EDGE,"E30.0");var subQ3=sQuery(id+"F0.wireOp",EDGE,"E63");var subQ4=makeQuery(id+"F0.imprint","INTERSECT",VERTEX,{"derivedFrom":[subQ1,subQ3]});Q32=makeQuery(id+"F0.imprint","IMPRINT",FACE,{"disambiguationData":[TD([[makeQuery(id+"F0.imprint","IMPRINT",EDGE,{"disambiguationData":[TD([[subQ4,-1.0]])],"derivedFrom":subQ3}),-1.0]])]});}
            var Q33;
            {var subQ1=sQuery(id+"F0.wireOp",EDGE,"E30.0");var subQ3=sQuery(id+"F0.wireOp",EDGE,"E34.trimOffspring");var subQ4=makeQuery(id+"F0.imprint","INTERSECT",VERTEX,{"derivedFrom":[subQ1,subQ3]});Q33=makeQuery(id+"F0.imprint","IMPRINT",FACE,{"disambiguationData":[TD([[makeQuery(id+"F0.imprint","IMPRINT",EDGE,{"disambiguationData":[TD([[subQ4,1.0]])],"derivedFrom":subQ3}),-1.0]])]});}
            var Q34;
            {var subQ0=sQuery(id+"F0.wireOp",EDGE,"E47.1");var subQ1=sQuery(id+"F0.wireOp",EDGE,"E30.0");var subQ2=makeQuery(id+"F0.imprint","INTERSECT",VERTEX,{"derivedFrom":[subQ1,subQ0]});Q34=makeQuery(id+"F0.imprint","IMPRINT",FACE,{"disambiguationData":[TD([[makeQuery(id+"F0.imprint","IMPRINT",EDGE,{"disambiguationData":[TD([[subQ2,1.0]])],"derivedFrom":subQ1}),1.0]])]});}
            var Q35;
            {var subQ0=sQuery(id+"F0.wireOp",EDGE,"E95");Q35=makeQuery(id+"F0.imprint","IMPRINT",FACE,{"disambiguationData":[TD([[makeQuery(id+"F0.imprint","IMPRINT",EDGE,{"derivedFrom":subQ0}),-1.0]])]});}
            var Q36;
            {var subQ0=sQuery(id+"F0.wireOp",EDGE,"E97");Q36=makeQuery(id+"F0.imprint","IMPRINT",FACE,{"disambiguationData":[TD([[makeQuery(id+"F0.imprint","IMPRINT",EDGE,{"derivedFrom":subQ0}),-1.0]])]});}
            var Q37;
            {var subQ4=sQuery(id+"F0.wireOp",EDGE,"E92.0");Q37=makeQuery(id+"F0.imprint","IMPRINT",FACE,{"disambiguationData":[TD([[makeQuery(id+"F0.imprint","IMPRINT",EDGE,{"derivedFrom":subQ4}),-1.0]])]});}
            var Q38;
            {var subQ3=sQuery(id+"F0.wireOp",EDGE,"E91.0");Q38=makeQuery(id+"F0.imprint","IMPRINT",FACE,{"disambiguationData":[TD([[makeQuery(id+"F0.imprint","IMPRINT",EDGE,{"derivedFrom":subQ3}),-1.0]])]});}
            var Q39;
            {var subQ2=sQuery(id+"F0.wireOp",EDGE,"E90.top");Q39=makeQuery(id+"F0.imprint","IMPRINT",FACE,{"disambiguationData":[TD([[makeQuery(id+"F0.imprint","IMPRINT",EDGE,{"derivedFrom":subQ2}),1.0]])]});}
            var Q40;
            {var subQ0=sQuery(id+"F0.wireOp",EDGE,"E90.bottom");Q40=makeQuery(id+"F0.imprint","IMPRINT",FACE,{"disambiguationData":[TD([[makeQuery(id+"F0.imprint","IMPRINT",EDGE,{"derivedFrom":subQ0}),-1.0]])]});}
            var Q41;
            {var subQ4=sQuery(id+"F0.wireOp",EDGE,"E47.2");var subQ5=sQuery(id+"F0.wireOp",EDGE,"E16.0");var subQ6=makeQuery(id+"F0.imprint","INTERSECT",VERTEX,{"derivedFrom":[subQ5,subQ4]});Q41=makeQuery(id+"F0.imprint","IMPRINT",FACE,{"disambiguationData":[TD([[makeQuery(id+"F0.imprint","IMPRINT",EDGE,{"disambiguationData":[TD([[subQ6,-1.0]])],"derivedFrom":subQ4}),-1.0]])]});}
            var Q42;
            {var subQ0=sQuery(id+"F0.wireOp",EDGE,"E75");Q42=makeQuery(id+"F0.imprint","IMPRINT",FACE,{"disambiguationData":[TD([[makeQuery(id+"F0.imprint","IMPRINT",EDGE,{"derivedFrom":subQ0}),-1.0]])]});}
            var Q43;
            {var subQ3=sQuery(id+"F0.wireOp",EDGE,"E35.trimOffspring");var subQ5=sQuery(id+"F0.wireOp",EDGE,"E48.0");var subQ6=makeQuery(id+"F0.imprint","INTERSECT",VERTEX,{"derivedFrom":[subQ3,subQ5]});Q43=makeQuery(id+"F0.imprint","IMPRINT",FACE,{"disambiguationData":[TD([[makeQuery(id+"F0.imprint","IMPRINT",EDGE,{"disambiguationData":[TD([[subQ6,1.0]])],"derivedFrom":subQ5}),-1.0]])]});}
            var Q44;
            {var subQ3=sQuery(id+"F0.wireOp",EDGE,"E36.trimOffspring");var subQ5=sQuery(id+"F0.wireOp",EDGE,"E48.0");var subQ6=makeQuery(id+"F0.imprint","INTERSECT",VERTEX,{"derivedFrom":[subQ3,subQ5]});Q44=makeQuery(id+"F0.imprint","IMPRINT",FACE,{"disambiguationData":[TD([[makeQuery(id+"F0.imprint","IMPRINT",EDGE,{"disambiguationData":[TD([[subQ6,1.0]])],"derivedFrom":subQ3}),1.0]])]});}
            var Q45;
            {var subQ0=sQuery(id+"F0.wireOp",EDGE,"E26.0");var subQ1=sQuery(id+"F0.wireOp",EDGE,"E19.0");var subQ2=makeQuery(id+"F0.imprint","INTERSECT",VERTEX,{"derivedFrom":[subQ1,subQ0]});Q45=makeQuery(id+"F0.imprint","IMPRINT",FACE,{"disambiguationData":[TD([[makeQuery(id+"F0.imprint","IMPRINT",EDGE,{"disambiguationData":[TD([[subQ2,1.0]])],"derivedFrom":subQ1}),-1.0]])]});}
            var Q46;
            {var subQ0=sQuery(id+"F0.wireOp",EDGE,"E48.0");var subQ1=sQuery(id+"F0.wireOp",EDGE,"E35.trimOffspring");var subQ2=makeQuery(id+"F0.imprint","INTERSECT",VERTEX,{"derivedFrom":[subQ1,subQ0]});Q46=makeQuery(id+"F0.imprint","IMPRINT",FACE,{"disambiguationData":[TD([[makeQuery(id+"F0.imprint","IMPRINT",EDGE,{"disambiguationData":[TD([[subQ2,-1.0]])],"derivedFrom":subQ1}),1.0]])]});}
            var Q47;
            {var subQ0=sQuery(id+"F0.wireOp",EDGE,"E30.0");var subQ1=sQuery(id+"F0.wireOp",EDGE,"E17.0");var subQ2=makeQuery(id+"F0.imprint","INTERSECT",VERTEX,{"derivedFrom":[subQ1,subQ0]});Q47=makeQuery(id+"F0.imprint","IMPRINT",FACE,{"disambiguationData":[TD([[makeQuery(id+"F0.imprint","IMPRINT",EDGE,{"disambiguationData":[TD([[subQ2,-1.0]])],"derivedFrom":subQ1}),-1.0]])]});}
            var Q48;
            {var subQ1=sQuery(id+"F0.wireOp",EDGE,"E30.0");var subQ3=sQuery(id+"F0.wireOp",EDGE,"E31.trimOffspring");var subQ4=makeQuery(id+"F0.imprint","INTERSECT",VERTEX,{"derivedFrom":[subQ1,subQ3]});Q48=makeQuery(id+"F0.imprint","IMPRINT",FACE,{"disambiguationData":[TD([[makeQuery(id+"F0.imprint","IMPRINT",EDGE,{"disambiguationData":[TD([[subQ4,1.0]])],"derivedFrom":subQ3}),1.0]])]});}
            var Q49;
            {var subQ0=sQuery(id+"F0.wireOp",EDGE,"E99");var subQ1=sQuery(id+"F0.wireOp",EDGE,"E31.trimOffspring");var subQ2=makeQuery(id+"F0.imprint","INTERSECT",VERTEX,{"derivedFrom":[subQ1,subQ0]});Q49=makeQuery(id+"F0.imprint","IMPRINT",FACE,{"disambiguationData":[TD([[makeQuery(id+"F0.imprint","IMPRINT",EDGE,{"disambiguationData":[TD([[subQ2,1.0]])],"derivedFrom":subQ1}),1.0]])]});}
            var Q50;
            {var subQ2=sQuery(id+"F0.wireOp",EDGE,"E17.0");var subQ4=sQuery(id+"F0.wireOp",EDGE,"E99");var subQ10=makeQuery(id+"F0.imprint","INTERSECT",VERTEX,{"derivedFrom":[subQ2,subQ4]});Q50=makeQuery(id+"F0.imprint","IMPRINT",FACE,{"disambiguationData":[TD([[makeQuery(id+"F0.imprint","IMPRINT",EDGE,{"disambiguationData":[TD([[subQ10,-1.0]])],"derivedFrom":subQ2}),-1.0]])]});}
            var Q51;
            {var subQ0=sQuery(id+"F0.wireOp",EDGE,"E101.0");var subQ1=sQuery(id+"F0.wireOp",EDGE,"E31.trimOffspring");var subQ2=makeQuery(id+"F0.imprint","INTERSECT",VERTEX,{"derivedFrom":[subQ1,subQ0]});Q51=makeQuery(id+"F0.imprint","IMPRINT",FACE,{"disambiguationData":[TD([[makeQuery(id+"F0.imprint","IMPRINT",EDGE,{"disambiguationData":[TD([[subQ2,1.0]])],"derivedFrom":subQ1}),1.0]])]});}
            var Q52;
            {var subQ4=sQuery(id+"F0.wireOp",EDGE,"E17.0");var subQ8=sQuery(id+"F0.wireOp",EDGE,"E102.0");var subQ10=makeQuery(id+"F0.imprint","INTERSECT",VERTEX,{"derivedFrom":[subQ4,subQ8]});Q52=makeQuery(id+"F0.imprint","IMPRINT",FACE,{"disambiguationData":[TD([[makeQuery(id+"F0.imprint","IMPRINT",EDGE,{"disambiguationData":[TD([[subQ10,1.0]])],"derivedFrom":subQ4}),-1.0]])]});}
            var Q53;
            {var subQ0=sQuery(id+"F0.wireOp",EDGE,"E104");Q53=makeQuery(id+"F0.imprint","IMPRINT",FACE,{"disambiguationData":[TD([[makeQuery(id+"F0.imprint","IMPRINT",EDGE,{"derivedFrom":subQ0}),-1.0]])]});}
            var Q54;
            {var subQ2=sQuery(id+"F0.wireOp",EDGE,"E103");Q54=makeQuery(id+"F0.imprint","IMPRINT",FACE,{"disambiguationData":[TD([[makeQuery(id+"F0.imprint","IMPRINT",EDGE,{"derivedFrom":subQ2}),1.0]])]});}
            var Q55;
            {var subQ0=sQuery(id+"F0.wireOp",EDGE,"E35.trimOffspring");var subQ5=sQuery(id+"F0.wireOp",EDGE,"E51.0");var subQ6=makeQuery(id+"F0.imprint","INTERSECT",VERTEX,{"derivedFrom":[subQ0,subQ5]});Q55=makeQuery(id+"F0.imprint","IMPRINT",FACE,{"disambiguationData":[TD([[makeQuery(id+"F0.imprint","IMPRINT",EDGE,{"disambiguationData":[TD([[subQ6,1.0]])],"derivedFrom":subQ5}),1.0]])]});}
            var Q56;
            {var subQ1=sQuery(id+"F0.wireOp",EDGE,"E27.0");var subQ3=sQuery(id+"F0.wireOp",EDGE,"E36.trimOffspring");var subQ4=makeQuery(id+"F0.imprint","INTERSECT",VERTEX,{"derivedFrom":[subQ1,subQ3]});Q56=makeQuery(id+"F0.imprint","IMPRINT",FACE,{"disambiguationData":[TD([[makeQuery(id+"F0.imprint","IMPRINT",EDGE,{"disambiguationData":[TD([[subQ4,1.0]])],"derivedFrom":subQ3}),1.0]])]});}
            var Q57;
            {var subQ0=sQuery(id+"F0.wireOp",EDGE,"E51.0");var subQ1=sQuery(id+"F0.wireOp",EDGE,"E19.0");var subQ2=makeQuery(id+"F0.imprint","INTERSECT",VERTEX,{"derivedFrom":[subQ1,subQ0]});Q57=makeQuery(id+"F0.imprint","IMPRINT",FACE,{"disambiguationData":[TD([[makeQuery(id+"F0.imprint","IMPRINT",EDGE,{"disambiguationData":[TD([[subQ2,1.0]])],"derivedFrom":subQ1}),-1.0]])]});}
            var Q58;
            {var subQ2=sQuery(id+"F0.wireOp",EDGE,"E73");Q58=makeQuery(id+"F0.imprint","IMPRINT",FACE,{"disambiguationData":[TD([[makeQuery(id+"F0.imprint","IMPRINT",EDGE,{"derivedFrom":subQ2}),-1.0]])]});}
            var Q59;
            {var subQ4=sQuery(id+"F0.wireOp",EDGE,"E41.trimOffspring");Q59=makeQuery(id+"F0.imprint","IMPRINT",FACE,{"disambiguationData":[TD([[makeQuery(id+"F0.imprint","IMPRINT",EDGE,{"derivedFrom":subQ4}),1.0]])]});}
            var Q60;
            {var subQ3=sQuery(id+"F0.wireOp",EDGE,"E120.0");Q60=makeQuery(id+"F0.imprint","IMPRINT",FACE,{"disambiguationData":[TD([[makeQuery(id+"F0.imprint","IMPRINT",EDGE,{"derivedFrom":subQ3}),1.0]])]});}
            var Q61;
            {var subQ2=sQuery(id+"F0.wireOp",EDGE,"E118");Q61=makeQuery(id+"F0.imprint","IMPRINT",FACE,{"disambiguationData":[TD([[makeQuery(id+"F0.imprint","IMPRINT",EDGE,{"derivedFrom":subQ2}),-1.0]])]});}
            var Q62;
            {var subQ6=sQuery(id+"F0.wireOp",EDGE,"E121.0");Q62=makeQuery(id+"F0.imprint","IMPRINT",FACE,{"disambiguationData":[TD([[makeQuery(id+"F0.imprint","IMPRINT",EDGE,{"derivedFrom":subQ6}),-1.0]])]});}
            var Q63;
            {var subQ0=sQuery(id+"F0.wireOp",EDGE,"E119");Q63=makeQuery(id+"F0.imprint","IMPRINT",FACE,{"disambiguationData":[TD([[makeQuery(id+"F0.imprint","IMPRINT",EDGE,{"derivedFrom":subQ0}),1.0]])]});}
            var Q64;
            {var subQ3=sQuery(id+"F0.wireOp",EDGE,"E111");Q64=makeQuery(id+"F0.imprint","IMPRINT",FACE,{"disambiguationData":[TD([[makeQuery(id+"F0.imprint","IMPRINT",EDGE,{"derivedFrom":subQ3}),-1.0]])]});}
            var Q65;
            {var subQ0=sQuery(id+"F0.wireOp",EDGE,"E108.0");var subQ1=sQuery(id+"F0.wireOp",EDGE,"E11.0");var subQ2=makeQuery(id+"F0.imprint","INTERSECT",VERTEX,{"derivedFrom":[subQ1,subQ0]});Q65=makeQuery(id+"F0.imprint","IMPRINT",FACE,{"disambiguationData":[TD([[makeQuery(id+"F0.imprint","IMPRINT",EDGE,{"disambiguationData":[TD([[subQ2,1.0]])],"derivedFrom":subQ1}),1.0]])]});}
            var Q66;
            {var subQ0=sQuery(id+"F0.wireOp",EDGE,"E108.0");var subQ8=sQuery(id+"F0.wireOp",EDGE,"E11.0");var subQ9=makeQuery(id+"F0.imprint","INTERSECT",VERTEX,{"derivedFrom":[subQ8,subQ0]});Q66=makeQuery(id+"F0.imprint","IMPRINT",FACE,{"disambiguationData":[TD([[makeQuery(id+"F0.imprint","IMPRINT",EDGE,{"disambiguationData":[TD([[subQ9,1.0]])],"derivedFrom":subQ8}),-1.0]])]});}
            var Q67;
            {var subQ0=sQuery(id+"F0.wireOp",EDGE,"E113.0");Q67=makeQuery(id+"F0.imprint","IMPRINT",FACE,{"disambiguationData":[TD([[makeQuery(id+"F0.imprint","IMPRINT",EDGE,{"derivedFrom":subQ0}),-1.0]])]});}
            var Q68;
            {var subQ3=sQuery(id+"F0.wireOp",EDGE,"E110.0");var subQ8=sQuery(id+"F0.wireOp",EDGE,"E17.0");var subQ10=makeQuery(id+"F0.imprint","INTERSECT",VERTEX,{"derivedFrom":[subQ8,subQ3]});Q68=makeQuery(id+"F0.imprint","IMPRINT",FACE,{"disambiguationData":[TD([[makeQuery(id+"F0.imprint","IMPRINT",EDGE,{"disambiguationData":[TD([[subQ10,-1.0]])],"derivedFrom":subQ8}),-1.0]])]});}
            var Q69;
            {var subQ2=sQuery(id+"F0.wireOp",EDGE,"E112");Q69=makeQuery(id+"F0.imprint","IMPRINT",FACE,{"disambiguationData":[TD([[makeQuery(id+"F0.imprint","IMPRINT",EDGE,{"derivedFrom":subQ2}),1.0]])]});}
            var Q70;
            {var subQ0=sQuery(id+"F0.wireOp",EDGE,"E133");Q70=makeQuery(id+"F0.imprint","IMPRINT",FACE,{"disambiguationData":[TD([[makeQuery(id+"F0.imprint","IMPRINT",EDGE,{"derivedFrom":subQ0}),-1.0]])]});}
            var Q71;
            {var subQ2=sQuery(id+"F0.wireOp",EDGE,"E135");Q71=makeQuery(id+"F0.imprint","IMPRINT",FACE,{"disambiguationData":[TD([[makeQuery(id+"F0.imprint","IMPRINT",EDGE,{"derivedFrom":subQ2}),1.0]])]});}
            var Q72;
            {var subQ0=sQuery(id+"F0.wireOp",EDGE,"E139");var subQ1=sQuery(id+"F0.wireOp",EDGE,"E34.trimOffspring");var subQ2=makeQuery(id+"F0.imprint","INTERSECT",VERTEX,{"derivedFrom":[subQ1,subQ0]});Q72=makeQuery(id+"F0.imprint","IMPRINT",FACE,{"disambiguationData":[TD([[makeQuery(id+"F0.imprint","IMPRINT",EDGE,{"disambiguationData":[TD([[subQ2,1.0]])],"derivedFrom":subQ1}),1.0]])]});}
            var Q73;
            {var subQ0=sQuery(id+"F0.wireOp",EDGE,"E139");var subQ1=sQuery(id+"F0.wireOp",EDGE,"E33.trimOffspring");var subQ2=makeQuery(id+"F0.imprint","INTERSECT",VERTEX,{"derivedFrom":[subQ1,subQ0]});Q73=makeQuery(id+"F0.imprint","IMPRINT",FACE,{"disambiguationData":[TD([[makeQuery(id+"F0.imprint","IMPRINT",EDGE,{"disambiguationData":[TD([[subQ2,1.0]])],"derivedFrom":subQ1}),1.0]])]});}
            extrude(context, id + "F1", {"entities" : qUnion([Q0, Q1, Q2, Q3, Q4, Q5, Q6, Q7, Q8, Q9, Q10, Q11, Q12, Q13, Q14, Q15, Q16, Q17, Q18, Q19, Q20, Q21, Q22, Q23, Q24, Q25, Q26, Q27, Q28, Q29, Q30, Q31, Q32, Q33, Q34, Q35, Q36, Q37, Q38, Q39, Q40, Q41, Q42, Q43, Q44, Q45, Q46, Q47, Q48, Q49, Q50, Q51, Q52, Q53, Q54, Q55, Q56, Q57, Q58, Q59, Q60, Q61, Q62, Q63, Q64, Q65, Q66, Q67, Q68, Q69, Q70, Q71, Q72, Q73]), "depth" : 88.9 * mm, "offsetDistance" : 25.4 * mm});
        }
        {
            var Q0;
            {var subQ0=sQuery(id+"F0.wireOp",EDGE,"E67");var subQ5=sQuery(id+"F0.wireOp",EDGE,"E26.0");var subQ6=makeQuery(id+"F0.imprint","INTERSECT",VERTEX,{"derivedFrom":[subQ5,subQ0]});Q0=makeQuery(id+"F0.imprint","IMPRINT",FACE,{"disambiguationData":[TD([[makeQuery(id+"F0.imprint","IMPRINT",EDGE,{"disambiguationData":[TD([[subQ6,-1.0]])],"derivedFrom":subQ5}),-1.0]])]});}
            var Q1;
            {var subQ1=sQuery(id+"F0.wireOp",EDGE,"E128");Q1=makeQuery(id+"F0.imprint","IMPRINT",FACE,{"disambiguationData":[TD([[makeQuery(id+"F0.imprint","IMPRINT",EDGE,{"derivedFrom":subQ1}),-1.0]])]});}
            var Q2;
            {var subQ6=sQuery(id+"F0.wireOp",EDGE,"E75");Q2=makeQuery(id+"F0.imprint","IMPRINT",FACE,{"disambiguationData":[TD([[makeQuery(id+"F0.imprint","IMPRINT",EDGE,{"derivedFrom":subQ6}),1.0]])]});}
            var Q3;
            {var subQ5=sQuery(id+"F0.wireOp",EDGE,"E98");Q3=makeQuery(id+"F0.imprint","IMPRINT",FACE,{"disambiguationData":[TD([[makeQuery(id+"F0.imprint","IMPRINT",EDGE,{"derivedFrom":subQ5}),-1.0]])]});}
            var Q4;
            {var subQ0=sQuery(id+"F0.wireOp",EDGE,"E51.0");var subQ5=sQuery(id+"F0.wireOp",EDGE,"E40.trimOffspring");var subQ6=makeQuery(id+"F0.imprint","INTERSECT",VERTEX,{"derivedFrom":[subQ5,subQ0]});Q4=makeQuery(id+"F0.imprint","IMPRINT",FACE,{"disambiguationData":[TD([[makeQuery(id+"F0.imprint","IMPRINT",EDGE,{"disambiguationData":[TD([[subQ6,-1.0]])],"derivedFrom":subQ5}),-1.0]])]});}
            var Q5;
            {var subQ3=sQuery(id+"F0.wireOp",EDGE,"E71");Q5=makeQuery(id+"F0.imprint","IMPRINT",FACE,{"disambiguationData":[TD([[makeQuery(id+"F0.imprint","IMPRINT",EDGE,{"derivedFrom":subQ3}),1.0]])]});}
            var Q6;
            {var subQ0=sQuery(id+"F0.wireOp",EDGE,"E72");Q6=makeQuery(id+"F0.imprint","IMPRINT",FACE,{"disambiguationData":[TD([[makeQuery(id+"F0.imprint","IMPRINT",EDGE,{"derivedFrom":subQ0}),-1.0]])]});}
            var Q7;
            {var subQ0=sQuery(id+"F0.wireOp",EDGE,"E133");Q7=makeQuery(id+"F0.imprint","IMPRINT",FACE,{"disambiguationData":[TD([[makeQuery(id+"F0.imprint","IMPRINT",EDGE,{"derivedFrom":subQ0}),1.0]])]});}
            var Q8;
            {var subQ0=sQuery(id+"F0.wireOp",EDGE,"E134");Q8=makeQuery(id+"F0.imprint","IMPRINT",FACE,{"disambiguationData":[TD([[makeQuery(id+"F0.imprint","IMPRINT",EDGE,{"derivedFrom":subQ0}),-1.0]])]});}
            var Q9;
            {var subQ3=sQuery(id+"F0.wireOp",EDGE,"E135");Q9=makeQuery(id+"F0.imprint","IMPRINT",FACE,{"disambiguationData":[TD([[makeQuery(id+"F0.imprint","IMPRINT",EDGE,{"derivedFrom":subQ3}),-1.0]])]});}
            var Q10;
            {var subQ0=sQuery(id+"F0.wireOp",EDGE,"E18.0");var subQ1=sQuery(id+"F0.wireOp",EDGE,"E11.0");var subQ2=makeQuery(id+"F0.imprint","INTERSECT",VERTEX,{"derivedFrom":[subQ1,subQ0]});Q10=makeQuery(id+"F0.imprint","IMPRINT",FACE,{"disambiguationData":[TD([[makeQuery(id+"F0.imprint","IMPRINT",EDGE,{"disambiguationData":[TD([[subQ2,-1.0]])],"derivedFrom":subQ1}),1.0]])]});}
            var Q11;
            {var subQ3=sQuery(id+"F0.wireOp",EDGE,"E111");Q11=makeQuery(id+"F0.imprint","IMPRINT",FACE,{"disambiguationData":[TD([[makeQuery(id+"F0.imprint","IMPRINT",EDGE,{"derivedFrom":subQ3}),1.0]])]});}
            var Q12;
            {var subQ0=sQuery(id+"F0.wireOp",EDGE,"E110.0");var subQ1=sQuery(id+"F0.wireOp",EDGE,"E11.0");var subQ2=makeQuery(id+"F0.imprint","INTERSECT",VERTEX,{"derivedFrom":[subQ1,subQ0]});Q12=makeQuery(id+"F0.imprint","IMPRINT",FACE,{"disambiguationData":[TD([[makeQuery(id+"F0.imprint","IMPRINT",EDGE,{"disambiguationData":[TD([[subQ2,-1.0]])],"derivedFrom":subQ1}),1.0]])]});}
            var Q13;
            {var subQ4=sQuery(id+"F0.wireOp",EDGE,"E17.0");var subQ6=sQuery(id+"F0.wireOp",EDGE,"E27.0");var subQ7=makeQuery(id+"F0.imprint","INTERSECT",VERTEX,{"derivedFrom":[subQ4,subQ6]});Q13=makeQuery(id+"F0.imprint","IMPRINT",FACE,{"disambiguationData":[TD([[makeQuery(id+"F0.imprint","IMPRINT",EDGE,{"disambiguationData":[TD([[subQ7,-1.0]])],"derivedFrom":subQ4}),-1.0]])]});}
            var Q14;
            {var subQ0=sQuery(id+"F0.wireOp",EDGE,"E37.trimOffspring");Q14=makeQuery(id+"F0.imprint","IMPRINT",FACE,{"disambiguationData":[TD([[makeQuery(id+"F0.imprint","IMPRINT",EDGE,{"derivedFrom":subQ0}),1.0]])]});}
            var Q15;
            {var subQ0=sQuery(id+"F0.wireOp",EDGE,"E76");Q15=makeQuery(id+"F0.imprint","IMPRINT",FACE,{"disambiguationData":[TD([[makeQuery(id+"F0.imprint","IMPRINT",EDGE,{"derivedFrom":subQ0}),-1.0]])]});}
            var Q16;
            {var subQ0=sQuery(id+"F0.wireOp",EDGE,"E47.2");var subQ1=sQuery(id+"F0.wireOp",EDGE,"E15.0");var subQ2=makeQuery(id+"F0.imprint","INTERSECT",VERTEX,{"derivedFrom":[subQ1,subQ0]});Q16=makeQuery(id+"F0.imprint","IMPRINT",FACE,{"disambiguationData":[TD([[makeQuery(id+"F0.imprint","IMPRINT",EDGE,{"disambiguationData":[TD([[subQ2,-1.0]])],"derivedFrom":subQ1}),1.0]])]});}
            var Q17;
            {var subQ0=sQuery(id+"F0.wireOp",EDGE,"E48.0");var subQ1=sQuery(id+"F0.wireOp",EDGE,"E35.trimOffspring");var subQ2=makeQuery(id+"F0.imprint","INTERSECT",VERTEX,{"derivedFrom":[subQ1,subQ0]});Q17=makeQuery(id+"F0.imprint","IMPRINT",FACE,{"disambiguationData":[TD([[makeQuery(id+"F0.imprint","IMPRINT",EDGE,{"disambiguationData":[TD([[subQ2,-1.0]])],"derivedFrom":subQ1}),-1.0]])]});}
            var Q18;
            {var subQ4=sQuery(id+"F0.wireOp",EDGE,"E74");Q18=makeQuery(id+"F0.imprint","IMPRINT",FACE,{"disambiguationData":[TD([[makeQuery(id+"F0.imprint","IMPRINT",EDGE,{"derivedFrom":subQ4}),-1.0]])]});}
            var Q19;
            {var subQ0=sQuery(id+"F0.wireOp",EDGE,"E41.trimOffspring");Q19=makeQuery(id+"F0.imprint","IMPRINT",FACE,{"disambiguationData":[TD([[makeQuery(id+"F0.imprint","IMPRINT",EDGE,{"derivedFrom":subQ0}),-1.0]])]});}
            var Q20;
            {var subQ2=sQuery(id+"F0.wireOp",EDGE,"E96");Q20=makeQuery(id+"F0.imprint","IMPRINT",FACE,{"disambiguationData":[TD([[makeQuery(id+"F0.imprint","IMPRINT",EDGE,{"derivedFrom":subQ2}),-1.0]])]});}
            var Q21;
            {var subQ0=sQuery(id+"F0.wireOp",EDGE,"E95");Q21=makeQuery(id+"F0.imprint","IMPRINT",FACE,{"disambiguationData":[TD([[makeQuery(id+"F0.imprint","IMPRINT",EDGE,{"derivedFrom":subQ0}),1.0]])]});}
            var Q22;
            {var subQ0=sQuery(id+"F0.wireOp",EDGE,"E64");Q22=makeQuery(id+"F0.imprint","IMPRINT",FACE,{"disambiguationData":[TD([[makeQuery(id+"F0.imprint","IMPRINT",EDGE,{"derivedFrom":subQ0}),-1.0]])]});}
            var Q23;
            {var subQ1=sQuery(id+"F0.wireOp",EDGE,"E29.0");var subQ3=sQuery(id+"F0.wireOp",EDGE,"E44.trimOffspring");var subQ4=makeQuery(id+"F0.imprint","INTERSECT",VERTEX,{"derivedFrom":[subQ1,subQ3]});Q23=makeQuery(id+"F0.imprint","IMPRINT",FACE,{"disambiguationData":[TD([[makeQuery(id+"F0.imprint","IMPRINT",EDGE,{"disambiguationData":[TD([[subQ4,-1.0]])],"derivedFrom":subQ3}),-1.0]])]});}
            var Q24;
            {var subQ0=sQuery(id+"F0.wireOp",EDGE,"E58");var subQ5=sQuery(id+"F0.wireOp",EDGE,"E30.0");var subQ6=makeQuery(id+"F0.imprint","INTERSECT",VERTEX,{"derivedFrom":[subQ5,subQ0]});Q24=makeQuery(id+"F0.imprint","IMPRINT",FACE,{"disambiguationData":[TD([[makeQuery(id+"F0.imprint","IMPRINT",EDGE,{"disambiguationData":[TD([[subQ6,-1.0]])],"derivedFrom":subQ5}),-1.0]])]});}
            var Q25;
            {var subQ0=sQuery(id+"F0.wireOp",EDGE,"E45.trimOffspring");var subQ1=sQuery(id+"F0.wireOp",EDGE,"E29.0");var subQ2=makeQuery(id+"F0.imprint","INTERSECT",VERTEX,{"derivedFrom":[subQ1,subQ0]});Q25=makeQuery(id+"F0.imprint","IMPRINT",FACE,{"disambiguationData":[TD([[makeQuery(id+"F0.imprint","IMPRINT",EDGE,{"disambiguationData":[TD([[subQ2,-1.0]])],"derivedFrom":subQ0}),1.0]])]});}
            var Q26;
            {var subQ7=sQuery(id+"F0.wireOp",EDGE,"E57");Q26=makeQuery(id+"F0.imprint","IMPRINT",FACE,{"disambiguationData":[TD([[makeQuery(id+"F0.imprint","IMPRINT",EDGE,{"derivedFrom":subQ7}),1.0]])]});}
            var Q27;
            {var subQ0=sQuery(id+"F0.wireOp",EDGE,"E99");var subQ1=sQuery(id+"F0.wireOp",EDGE,"E31.trimOffspring");var subQ2=makeQuery(id+"F0.imprint","INTERSECT",VERTEX,{"derivedFrom":[subQ1,subQ0]});Q27=makeQuery(id+"F0.imprint","IMPRINT",FACE,{"disambiguationData":[TD([[makeQuery(id+"F0.imprint","IMPRINT",EDGE,{"disambiguationData":[TD([[subQ2,-1.0]])],"derivedFrom":subQ1}),1.0]])]});}
            var Q28;
            {var subQ0=sQuery(id+"F0.wireOp",EDGE,"E101.0");var subQ1=sQuery(id+"F0.wireOp",EDGE,"E31.trimOffspring");var subQ2=makeQuery(id+"F0.imprint","INTERSECT",VERTEX,{"derivedFrom":[subQ1,subQ0]});Q28=makeQuery(id+"F0.imprint","IMPRINT",FACE,{"disambiguationData":[TD([[makeQuery(id+"F0.imprint","IMPRINT",EDGE,{"disambiguationData":[TD([[subQ2,-1.0]])],"derivedFrom":subQ1}),1.0]])]});}
            var Q29;
            {var subQ0=sQuery(id+"F0.wireOp",EDGE,"E31.trimOffspring");var subQ5=sQuery(id+"F0.wireOp",EDGE,"E102.0");var subQ6=makeQuery(id+"F0.imprint","INTERSECT",VERTEX,{"derivedFrom":[subQ0,subQ5]});Q29=makeQuery(id+"F0.imprint","IMPRINT",FACE,{"disambiguationData":[TD([[makeQuery(id+"F0.imprint","IMPRINT",EDGE,{"disambiguationData":[TD([[subQ6,1.0]])],"derivedFrom":subQ0}),1.0]])]});}
            var Q30;
            {var subQ0=sQuery(id+"F0.wireOp",EDGE,"E25.0");var subQ5=sQuery(id+"F0.wireOp",EDGE,"E17.0");var subQ8=makeQuery(id+"F0.imprint","INTERSECT",VERTEX,{"derivedFrom":[subQ5,subQ0]});Q30=makeQuery(id+"F0.imprint","IMPRINT",FACE,{"disambiguationData":[TD([[makeQuery(id+"F0.imprint","IMPRINT",EDGE,{"disambiguationData":[TD([[subQ8,-1.0]])],"derivedFrom":subQ5}),-1.0]])]});}
            var Q31;
            {var subQ0=sQuery(id+"F0.wireOp",EDGE,"E140.0");var subQ1=sQuery(id+"F0.wireOp",EDGE,"E33.trimOffspring");var subQ2=makeQuery(id+"F0.imprint","INTERSECT",VERTEX,{"derivedFrom":[subQ1,subQ0]});Q31=makeQuery(id+"F0.imprint","IMPRINT",FACE,{"disambiguationData":[TD([[makeQuery(id+"F0.imprint","IMPRINT",EDGE,{"disambiguationData":[TD([[subQ2,1.0]])],"derivedFrom":subQ1}),1.0]])]});}
            var Q32;
            {var subQ0=sQuery(id+"F0.wireOp",EDGE,"E139");var subQ1=sQuery(id+"F0.wireOp",EDGE,"E33.trimOffspring");var subQ2=makeQuery(id+"F0.imprint","INTERSECT",VERTEX,{"derivedFrom":[subQ1,subQ0]});Q32=makeQuery(id+"F0.imprint","IMPRINT",FACE,{"disambiguationData":[TD([[makeQuery(id+"F0.imprint","IMPRINT",EDGE,{"disambiguationData":[TD([[subQ2,-1.0]])],"derivedFrom":subQ1}),1.0]])]});}
            extrude(context, id + "F2", {"entities" : qUnion([Q0, Q1, Q2, Q3, Q4, Q5, Q6, Q7, Q8, Q9, Q10, Q11, Q12, Q13, Q14, Q15, Q16, Q17, Q18, Q19, Q20, Q21, Q22, Q23, Q24, Q25, Q26, Q27, Q28, Q29, Q30, Q31, Q32]), "operationType" : NewBodyOperationType.ADD, "depth" : 38.1 * mm, "offsetDistance" : 25.4 * mm});
        }
        {
            var Q0;
            {var subQ1=sQuery(id+"F0.wireOp",EDGE,"E47.1");var subQ4=makeQuery(id+"F0.imprint","INTERSECT",VERTEX,{"derivedFrom":[subQ1,sQuery(id+"F0.wireOp",EDGE,"E139")]});var subQ7=sQuery(id+"F0.wireOp",EDGE,"E5");var subQ8=sQuery(id+"F0.wireOp",EDGE,"E0");var subQ13=sQuery(id+"F0.wireOp",EDGE,"E43.trimOffspring");var subQ14=sQuery(id+"F0.wireOp",EDGE,"E1");var subQ15=makeQuery(id+"F0.imprint","INTERSECT",VERTEX,{"derivedFrom":[subQ14,subQ13]});var subQ23=sQuery(id+"F0.wireOp",EDGE,"E2");var subQ24=makeQuery(id+"F0.imprint","INTERSECT",VERTEX,{"derivedFrom":[subQ14,subQ23]});var subQ31=sQuery(id+"F0.wireOp",EDGE,"E53.0");var subQ32=makeQuery(id+"F0.imprint","INTERSECT",VERTEX,{"derivedFrom":[subQ14,subQ31]});var subQ39=sQuery(id+"F0.wireOp",EDGE,"E19.0");var subQ40=makeQuery(id+"F0.imprint","INTERSECT",VERTEX,{"derivedFrom":[subQ7,subQ39]});var subQ41=sQuery(id+"F0.wireOp",EDGE,"E15.0");var subQ42=makeQuery(id+"F0.imprint","INTERSECT",VERTEX,{"derivedFrom":[subQ7,subQ41]});var subQ48=sQuery(id+"F0.wireOp",EDGE,"E46.trimOffspring");var subQ49=makeQuery(id+"F0.imprint","INTERSECT",VERTEX,{"derivedFrom":[subQ14,subQ48]});var subQ52=sQuery(id+"F0.wireOp",EDGE,"E21");var subQ53=makeQuery(id+"F0.imprint","IMPRINT",EDGE,{"derivedFrom":subQ52});var subQ54=sQuery(id+"F0.wireOp",EDGE,"E4");var subQ74=sQuery(id+"F0.wireOp",EDGE,"E45.trimOffspring");var subQ75=makeQuery(id+"F0.imprint","INTERSECT",VERTEX,{"derivedFrom":[subQ14,subQ74]});var subQ90=sQuery(id+"F0.wireOp",EDGE,"E22");var subQ94=makeQuery(id+"F0.imprint","IMPRINT",EDGE,{"derivedFrom":subQ90});var subQ95=sQuery(id+"F0.wireOp",EDGE,"E30.0");var subQ96=makeQuery(id+"F0.imprint","INTERSECT",VERTEX,{"derivedFrom":[subQ8,subQ95]});var subQ99=sQuery(id+"F0.wireOp",EDGE,"E60.0");var subQ100=makeQuery(id+"F0.imprint","INTERSECT",VERTEX,{"derivedFrom":[subQ7,subQ99]});var subQ102=makeQuery(id+"F0.imprint","IMPRINT",EDGE,{"disambiguationData":[TD([[subQ100,-1.0]])],"derivedFrom":subQ99});var subQ103=sQuery(id+"F0.wireOp",EDGE,"E29.0");var subQ104=makeQuery(id+"F0.imprint","INTERSECT",VERTEX,{"derivedFrom":[subQ8,subQ103]});var subQ110=makeQuery(id+"F0.imprint","INTERSECT",VERTEX,{"derivedFrom":[subQ54,subQ7]});Q0=qUnion([makeQuery(id+"F0.imprint","IMPRINT",FACE,{"disambiguationData":[TD([[subQ94,1.0]])]}),makeQuery(id+"F0.imprint","IMPRINT",FACE,{"disambiguationData":[TD([[makeQuery(id+"F0.imprint","IMPRINT",EDGE,{"disambiguationData":[TD([[subQ110,1.0]])],"derivedFrom":subQ54}),-1.0]])]}),makeQuery(id+"F0.imprint","IMPRINT",FACE,{"disambiguationData":[TD([[subQ102,1.0]])]}),makeQuery(id+"F0.imprint","IMPRINT",FACE,{"disambiguationData":[TD([[makeQuery(id+"F0.imprint","IMPRINT",EDGE,{"disambiguationData":[TD([[subQ104,-1.0]])],"derivedFrom":subQ8}),-1.0]])]}),makeQuery(id+"F0.imprint","IMPRINT",FACE,{"disambiguationData":[TD([[makeQuery(id+"F0.imprint","IMPRINT",EDGE,{"disambiguationData":[TD([[subQ96,-1.0]])],"derivedFrom":subQ8}),-1.0]])]}),makeQuery(id+"F0.imprint","IMPRINT",FACE,{"disambiguationData":[TD([[makeQuery(id+"F0.imprint","IMPRINT",EDGE,{"disambiguationData":[TD([[subQ15,-1.0]])],"derivedFrom":subQ14}),-1.0]])]}),makeQuery(id+"F0.imprint","IMPRINT",FACE,{"disambiguationData":[TD([[makeQuery(id+"F0.imprint","IMPRINT",EDGE,{"disambiguationData":[TD([[subQ100,1.0]])],"derivedFrom":subQ7}),-1.0]])]}),makeQuery(id+"F0.imprint","IMPRINT",FACE,{"disambiguationData":[TD([[makeQuery(id+"F0.imprint","IMPRINT",EDGE,{"disambiguationData":[TD([[subQ96,1.0]])],"derivedFrom":subQ8}),-1.0]])]}),makeQuery(id+"F0.imprint","IMPRINT",FACE,{"disambiguationData":[TD([[subQ53,1.0]])]}),makeQuery(id+"F0.imprint","IMPRINT",FACE,{"disambiguationData":[TD([[makeQuery(id+"F0.imprint","IMPRINT",EDGE,{"disambiguationData":[TD([[subQ75,1.0]])],"derivedFrom":subQ14}),-1.0]])]}),makeQuery(id+"F0.imprint","IMPRINT",FACE,{"disambiguationData":[TD([[makeQuery(id+"F0.imprint","IMPRINT",EDGE,{"disambiguationData":[TD([[subQ42,-1.0]])],"derivedFrom":subQ7}),-1.0]])]}),makeQuery(id+"F0.imprint","IMPRINT",FACE,{"disambiguationData":[TD([[makeQuery(id+"F0.imprint","IMPRINT",EDGE,{"disambiguationData":[TD([[subQ75,-1.0]])],"derivedFrom":subQ14}),-1.0]])]}),makeQuery(id+"F0.imprint","IMPRINT",FACE,{"disambiguationData":[TD([[subQ53,-1.0]])]}),makeQuery(id+"F0.imprint","IMPRINT",FACE,{"disambiguationData":[TD([[makeQuery(id+"F0.imprint","IMPRINT",EDGE,{"disambiguationData":[TD([[subQ49,1.0]])],"derivedFrom":subQ14}),-1.0]])]}),makeQuery(id+"F0.imprint","IMPRINT",FACE,{"disambiguationData":[TD([[makeQuery(id+"F0.imprint","IMPRINT",EDGE,{"disambiguationData":[TD([[subQ40,-1.0]])],"derivedFrom":subQ7}),-1.0]])]}),makeQuery(id+"F0.imprint","IMPRINT",FACE,{"disambiguationData":[TD([[makeQuery(id+"F0.imprint","IMPRINT",EDGE,{"disambiguationData":[TD([[subQ32,1.0]])],"derivedFrom":subQ14}),-1.0]])]}),makeQuery(id+"F0.imprint","IMPRINT",FACE,{"disambiguationData":[TD([[makeQuery(id+"F0.imprint","IMPRINT",EDGE,{"disambiguationData":[TD([[subQ24,1.0]])],"derivedFrom":subQ14}),-1.0]])]}),makeQuery(id+"F0.imprint","IMPRINT",FACE,{"disambiguationData":[TD([[makeQuery(id+"F0.imprint","IMPRINT",EDGE,{"disambiguationData":[TD([[subQ15,1.0]])],"derivedFrom":subQ14}),-1.0]])]}),makeQuery(id+"F0.imprint","IMPRINT",FACE,{"disambiguationData":[TD([[makeQuery(id+"F0.imprint","IMPRINT",EDGE,{"disambiguationData":[TD([[subQ4,-1.0]])],"derivedFrom":subQ1}),1.0]])]})]);}
            var Q1;
            {var subQ0=sQuery(id+"F0.wireOp",EDGE,"E138");var subQ1=sQuery(id+"F0.wireOp",EDGE,"E34.trimOffspring");var subQ2=makeQuery(id+"F0.imprint","INTERSECT",VERTEX,{"derivedFrom":[subQ1,subQ0]});Q1=makeQuery(id+"F0.imprint","IMPRINT",FACE,{"disambiguationData":[TD([[makeQuery(id+"F0.imprint","IMPRINT",EDGE,{"disambiguationData":[TD([[subQ2,1.0]])],"derivedFrom":subQ1}),1.0]])]});}
            var Q2;
            {var subQ0=sQuery(id+"F0.wireOp",EDGE,"E137");var subQ1=sQuery(id+"F0.wireOp",EDGE,"E33.trimOffspring");var subQ2=makeQuery(id+"F0.imprint","INTERSECT",VERTEX,{"derivedFrom":[subQ1,subQ0]});Q2=makeQuery(id+"F0.imprint","IMPRINT",FACE,{"disambiguationData":[TD([[makeQuery(id+"F0.imprint","IMPRINT",EDGE,{"disambiguationData":[TD([[subQ2,-1.0]])],"derivedFrom":subQ1}),1.0]])]});}
            extrude(context, id + "F3", {"entities" : qUnion([Q0, Q1, Q2]), "operationType" : NewBodyOperationType.ADD, "depth" : 88.9 * mm, "offsetDistance" : 25.4 * mm});
        }
    });
